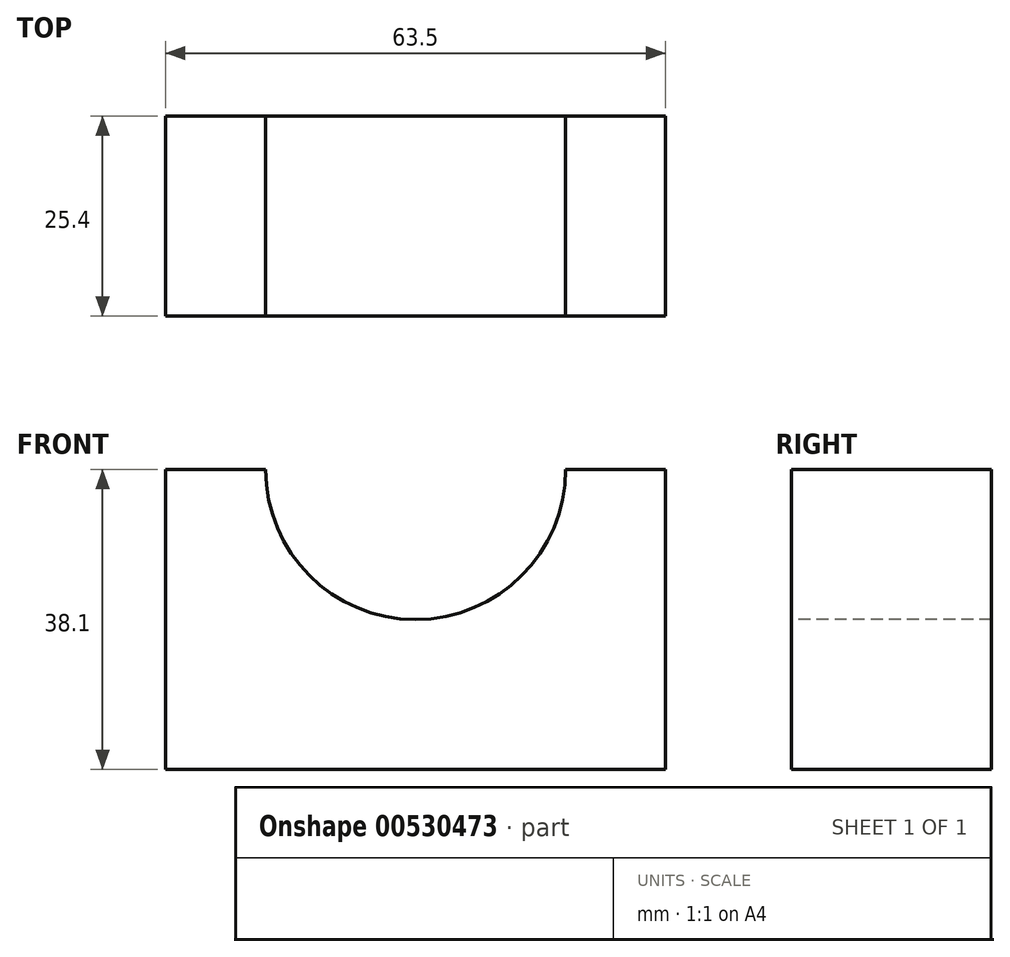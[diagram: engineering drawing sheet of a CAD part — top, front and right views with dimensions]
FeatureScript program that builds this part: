
annotation { "Feature Type Name" : "Feature", "Feature Type Description" : "" }
export const myFeature = defineFeature(function(context is Context, id is Id, definition is map)
    precondition{}
    {
        {
            var Q0;
            Q0=qCreatedBy(makeId("Front.planeOp"),FACE);
            var sketch = newSketch(context, id + "F0", { "sketchPlane" : qUnion([Q0])});
            skLineSegment(sketch, "E0", {"start": v(-74.86, 0) * mm, "end": v(-11.36, 0) * mm});
            skLineSegment(sketch, "E1", {"start": v(-11.36, 0) * mm, "end": v(-11.36, 38.1) * mm});
            skLineSegment(sketch, "E2", {"start": v(-74.86, 0) * mm, "end": v(-74.86, 38.1) * mm});
            skLineSegment(sketch, "E3", {"start": v(-74.86, 38.1) * mm, "end": v(-11.36, 38.1) * mm});
            skSolve(sketch);
        }
        {
            var Q0;
            Q0 = qSketchRegion(id + "F0", true);
            var Q1;
            Q1=makeQuery(id+"F0.imprint","IMPRINT",FACE,{"disambiguationData":[TD([[makeQuery(id+"F0.imprint","IMPRINT",EDGE,{"derivedFrom":sQuery(id+"F0.wireOp",EDGE,"E0")}),1.0]])]});
            extrude(context, id + "F1", {"entities" : qUnion([Q0, Q1]), "depth" : 25.4 * mm, "offsetDistance" : 25.4 * mm});
        }
        {
            var Q0;
            Q0=makeQuery(id+"F1.opExtrude","CAP_FACE",FACE,{"disambiguationData":[OSD([sQuery(id+"F0.wireOp",EDGE,"E0"),sQuery(id+"F0.wireOp",EDGE,"E1"),sQuery(id+"F0.wireOp",EDGE,"E2"),sQuery(id+"F0.wireOp",EDGE,"E3")])],"isStart":false});
            var sketch = newSketch(context, id + "F2", { "sketchPlane" : qUnion([Q0])});
            skArc(sketch, "E4", {"start": v(-62.16, 38.1) * mm, "mid": v(-43.1, 19.05) * mm, "end": v(-24.06, 38.1) * mm});
            skSolve(sketch);
        }
        {
            var Q0;
            Q0 = qSketchRegion(id + "F2", true);
            var Q1;
            {var subQ0=sQuery(id+"F2.wireOp",EDGE,"E4");Q1=makeQuery(id+"F2.imprint","IMPRINT",FACE,{"disambiguationData":[TD([[makeQuery(id+"F2.imprint","IMPRINT",EDGE,{"derivedFrom":subQ0}),1.0]])]});}
            extrude(context, id + "F3", {"entities" : qUnion([Q0, Q1]), "operationType" : NewBodyOperationType.REMOVE, "endBound" : BoundingType.THROUGH_ALL, "oppositeDirection" : true, "depth" : 25.4 * mm, "offsetDistance" : 25.4 * mm});
        }
    });
